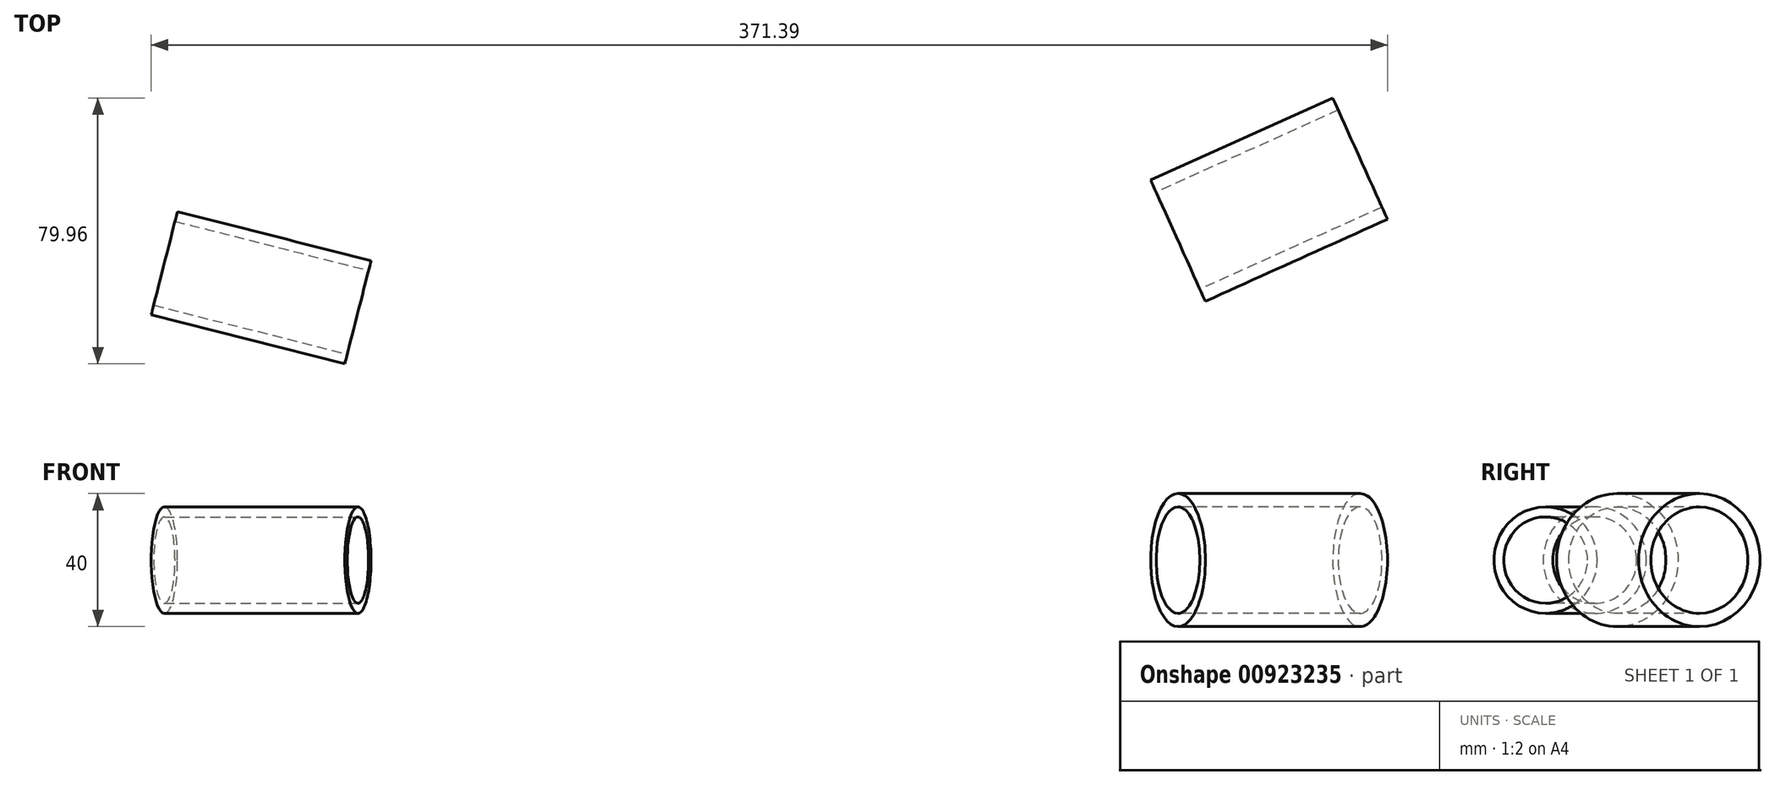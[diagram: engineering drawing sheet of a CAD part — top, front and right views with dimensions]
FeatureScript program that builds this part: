
annotation { "Feature Type Name" : "Feature", "Feature Type Description" : "" }
export const myFeature = defineFeature(function(context is Context, id is Id, definition is map)
    precondition{}
    {
        {
            var Q0;
            Q0=qCreatedBy(makeId("Top.planeOp"),FACE);
            var sketch = newSketch(context, id + "F0", { "sketchPlane" : qUnion([Q0])});
            skLineSegment(sketch, "E0", {"start": v(0, 0) * mm, "end": v(0, 67.8) * mm});
            skArc(sketch, "E1", {"start": v(190.53, 110) * mm, "mid": v(91.89, 60.84) * mm, "end": v(0, 0) * mm, "construction": true});
            skArc(sketch, "E2", {"start": v(0, 0) * mm, "mid": v(-101.06, 43.96) * mm, "end": v(-206.73, 75.24) * mm, "construction": true});
            skLineSegment(sketch, "E3", {"start": v(117.37, 77.28) * mm, "end": v(172.08, 101.93) * mm, "construction": true});
            skLineSegment(sketch, "E4", {"start": v(-129.01, 55.72) * mm, "end": v(-187.16, 70.5) * mm, "construction": true});
            skLineSegment(sketch, "E5", {"start": v(0, 0) * mm, "end": v(190.53, 110) * mm, "construction": true});
            skLineSegment(sketch, "E6", {"start": v(0, 0) * mm, "end": v(-206.73, 75.24) * mm, "construction": true});
            skLineSegment(sketch, "E7.0", {"start": v(-125.07, 71.23) * mm, "end": v(-183.22, 86) * mm});
            skLineSegment(sketch, "E8.0", {"start": v(-125.8, 68.32) * mm, "end": v(-183.96, 83.1) * mm});
            skLineSegment(sketch, "E9", {"start": v(-183.96, 83.1) * mm, "end": v(-183.22, 86) * mm});
            skLineSegment(sketch, "E10", {"start": v(-125.8, 68.32) * mm, "end": v(-125.07, 71.23) * mm});
            skLineSegment(sketch, "E11.0", {"start": v(109.16, 95.51) * mm, "end": v(163.86, 120.17) * mm});
            skLineSegment(sketch, "E12.0", {"start": v(110.8, 91.86) * mm, "end": v(165.5, 116.52) * mm});
            skLineSegment(sketch, "E13", {"start": v(110.8, 91.86) * mm, "end": v(109.16, 95.51) * mm});
            skLineSegment(sketch, "E14", {"start": v(165.5, 116.52) * mm, "end": v(163.86, 120.17) * mm});
            skLineSegment(sketch, "E15.0", {"start": v(-122.6, 80.92) * mm, "end": v(-180.76, 95.7) * mm, "construction": true});
            skLineSegment(sketch, "E16.0", {"start": v(100.49, 102.57) * mm, "end": v(159.75, 129.28) * mm, "construction": true});
            skLineSegment(sketch, "E17", {"start": v(-183.22, 86) * mm, "end": v(-180.76, 95.7) * mm});
            skLineSegment(sketch, "E18", {"start": v(163.86, 120.17) * mm, "end": v(159.75, 129.28) * mm});
            skArc(sketch, "E19", {"start": v(159.75, 129.28) * mm, "mid": v(-22.28, 231.94) * mm, "end": v(-180.76, 95.7) * mm});
            skLineSegment(sketch, "E20", {"start": v(100.49, 102.57) * mm, "end": v(44.24, 77.22) * mm});
            skLineSegment(sketch, "E21", {"start": v(-117.76, 79.69) * mm, "end": v(-10.68, 52.47) * mm});
            skLineSegment(sketch, "E22.0", {"start": v(20, 0) * mm, "end": v(20, 67.8) * mm});
            skLineSegment(sketch, "E23.0", {"start": v(-20, 0) * mm, "end": v(-20, 67.8) * mm});
            skLineSegment(sketch, "E24", {"start": v(165.5, 116.52) * mm, "end": v(172.08, 101.93) * mm, "construction": true});
            skLineSegment(sketch, "E25", {"start": v(109.16, 95.51) * mm, "end": v(107.1, 100.07) * mm, "construction": true});
            skArc(sketch, "E26.filletArc", {"start": v(107.1, 100.07) * mm, "mid": v(104.31, 102.7) * mm, "end": v(100.49, 102.57) * mm});
            skLineSegment(sketch, "E27", {"start": v(-125.07, 71.23) * mm, "end": v(-123.84, 76.07) * mm});
            skPoint(sketch, "E28.visualSharp", {"position": v(-122.6, 80.92) * mm});
            skArc(sketch, "E28.filletArc", {"start": v(-117.76, 79.69) * mm, "mid": v(-121.55, 79.14) * mm, "end": v(-123.84, 76.07) * mm});
            skArc(sketch, "E29.0", {"start": v(87.37, 184.28) * mm, "mid": v(-27.27, 211.2) * mm, "end": v(-129.83, 153.34) * mm, "construction": true});
            skLineSegment(sketch, "E30.0", {"start": v(94.33, 116.25) * mm, "end": v(153.58, 142.96) * mm, "construction": true});
            skLineSegment(sketch, "E31.0", {"start": v(-173.16, 109.25) * mm, "end": v(-231.3, 124.03) * mm, "construction": true});
            skCircle(sketch, "E32", {"center": v(134.37, 134.3) * mm, "radius": 4 * mm});
            skCircle(sketch, "E33", {"center": v(-157, 105.14) * mm, "radius": 4 * mm});
            skArc(sketch, "E34.0", {"start": v(64.7, 151.33) * mm, "mid": v(-21.63, 171.6) * mm, "end": v(-98.85, 128.03) * mm});
            skSolve(sketch);
        }
        {
            var Q0;
            Q0=makeQuery(id+"F0.imprint","IMPRINT",FACE,{"disambiguationData":[TD([[makeQuery(id+"F0.imprint","IMPRINT",EDGE,{"derivedFrom":sQuery(id+"F0.wireOp",EDGE,"E7.0")}),1.0]])]});
            var Q1;
            Q1=sQuery(id+"F0.wireOp",EDGE,"E4");
            revolve(context, id + "F1", {"surfaceOperationType" : NewSurfaceOperationType.NEW, "entities" : qUnion([Q0]), "axis" : qUnion([Q1]), "revolveType" : RevolveType.FULL});
        }
        {
            var Q0;
            Q0=makeQuery(id+"F0.imprint","IMPRINT",FACE,{"disambiguationData":[TD([[makeQuery(id+"F0.imprint","IMPRINT",EDGE,{"derivedFrom":sQuery(id+"F0.wireOp",EDGE,"E11.0")}),-1.0]])]});
            var Q1;
            Q1=sQuery(id+"F0.wireOp",EDGE,"E3");
            revolve(context, id + "F2", {"surfaceOperationType" : NewSurfaceOperationType.NEW, "entities" : qUnion([Q0]), "axis" : qUnion([Q1]), "revolveType" : RevolveType.FULL});
        }
    });
